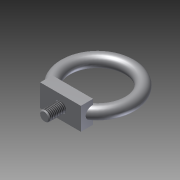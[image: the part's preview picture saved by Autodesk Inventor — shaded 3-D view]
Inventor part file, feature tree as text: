
AUTODESK INVENTOR PART (.ipt)
format: ipt  version: 2011 SP1 (Build 150282100, 282)  size: 162,816 bytes
history: native  units: mm
features: other x7, sketch x6, revolve x3, extrude x3, thread x1
ambient origin geometry x8: Origin, YZ Plane, XZ Plane, XY Plane, X Axis, Y Axis, Z Axis, Center Point
bodies: Solid1 (feature_tree)
feature tree (20):
  revolve  "Revolution1"  [1 undecoded]
  sketch  "Sketch_3"  dims[d6=360.0deg d7=10.0mm d8=1.29mm]
  extrude  "Extrusion1"  TaperAngle=360.0deg  [1 undecoded]
  extrude  "Extrusion2"  Depth=10.0mm
  revolve  "Revolution2"  [1 undecoded]
  revolve  "Revolution3"  [1 undecoded]
  thread  "Thread1"  [1 undecoded]
  extrude  "Extrusion3"  [1 undecoded]
  other  "side_1_XY"
  other  "side_1_YZ"
  other  "side_1_ZX"
  other  "side_1_X"
  other  "side_1_Y"
  other  "side_1_Z"
  other  "side_1_Center"
  sketch  "Sketch_1"  dims[d0=360.0deg d1=11.0mm d2=0.0mm]
  sketch  "Sketch_2"  dims[d3=11.0mm d4=0.0mm d5=360.0deg]
  sketch  "Sketch_4"  dims[d9=2.0mm d10=0.0mm]
  sketch  "Sketch_5"
  sketch  "Sketch_6"
note: 6 required parameter values undecoded (feature->parameter linkage not recoverable at this tier; creation-order binding heuristic only, values carry confidence <= 0.55)